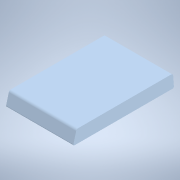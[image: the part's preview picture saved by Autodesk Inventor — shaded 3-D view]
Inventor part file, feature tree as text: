
AUTODESK INVENTOR PART (.ipt)
format: ipt  version: 2021 (Build 250183000, 183)  size: 113,152 bytes
history: native  units: mm
features: fillet x2, extrude x1, sketch x1
ambient origin geometry x8: Origin, YZ Plane, XZ Plane, XY Plane, X Axis, Y Axis, Z Axis, Center Point
bodies: Solid1 (feature_tree)
feature tree (4):
  extrude  "Extrusion1"  Depth=10.0mm
  fillet  "Fillet1"  [1 undecoded]
  fillet  "Fillet2"  Radius=430.0mm
  sketch  "Sketch1"  dims[d0=450.0mm d1=60.0mm d2=15.0deg d3=430.0mm d4=300.0mm d5=0.0mm d6=5.0mm d7=10.0mm]
note: 1 required parameter value undecoded (feature->parameter linkage not recoverable at this tier; creation-order binding heuristic only, values carry confidence <= 0.55)
